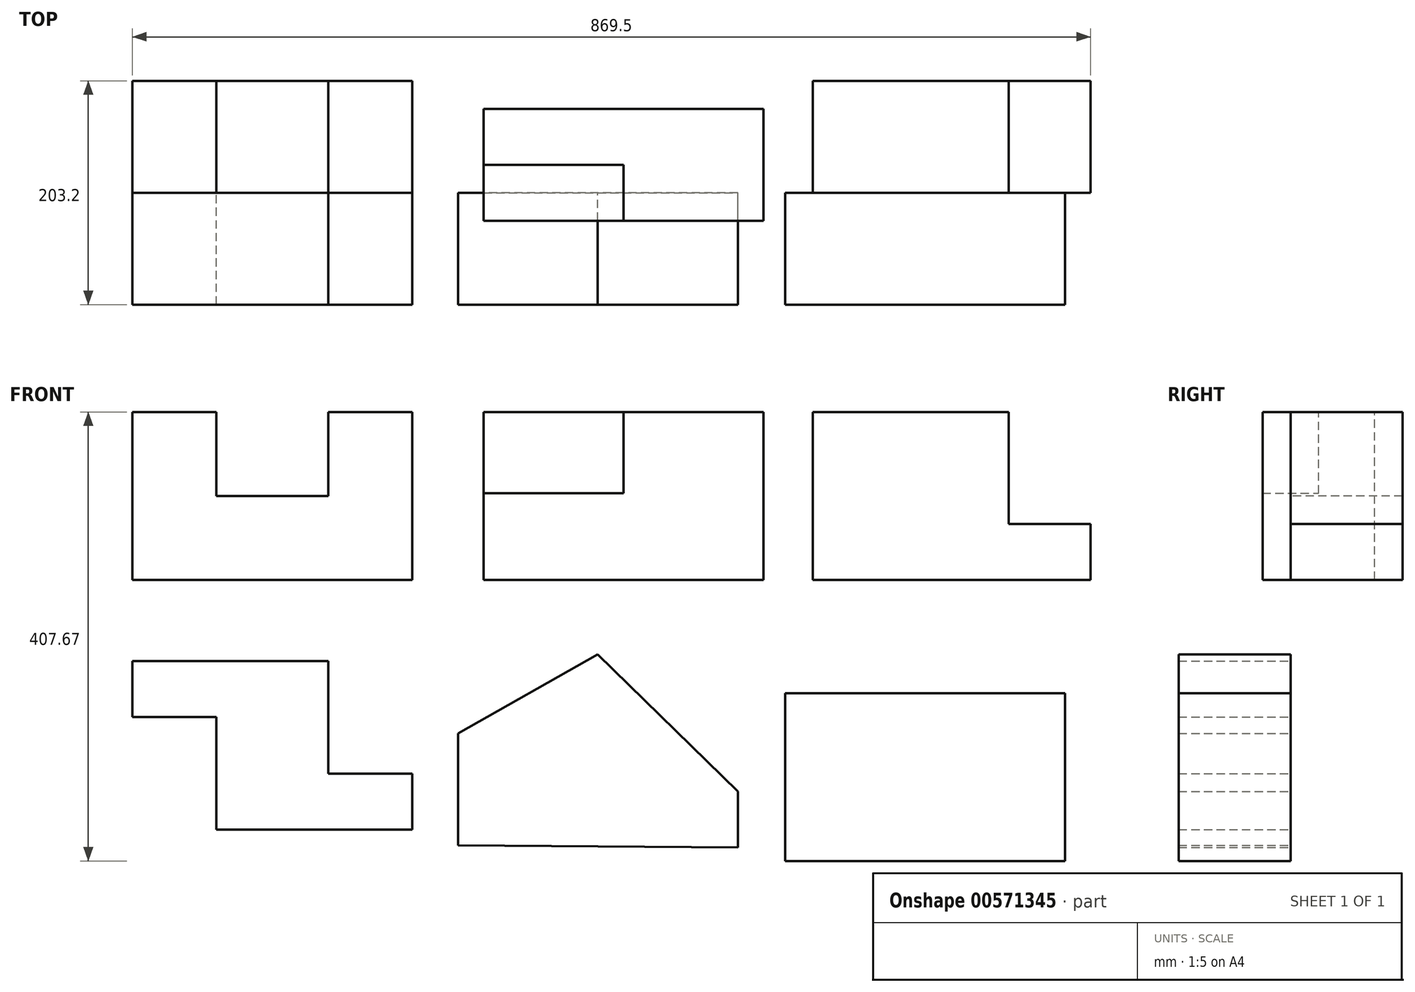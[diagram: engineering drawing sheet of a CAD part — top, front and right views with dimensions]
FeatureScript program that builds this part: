
annotation { "Feature Type Name" : "Feature", "Feature Type Description" : "" }
export const myFeature = defineFeature(function(context is Context, id is Id, definition is map)
    precondition{}
    {
        {
            var Q0;
            Q0=qCreatedBy(makeId("Front.planeOp"),FACE);
            var sketch = newSketch(context, id + "F0", { "sketchPlane" : qUnion([Q0])});
            skLineSegment(sketch, "E0", {"start": v(0, 0) * mm, "end": v(254, 0) * mm});
            skLineSegment(sketch, "E1", {"start": v(254, 0) * mm, "end": v(254, 152.4) * mm});
            skPoint(sketch, "E2.orphan", {"position": v(128.57, 246.94) * mm});
            skPoint(sketch, "E3.end.orphan", {"position": v(179.34, 246.94) * mm});
            skLineSegment(sketch, "E4", {"start": v(254, 152.4) * mm, "end": v(177.8, 152.4) * mm});
            skPoint(sketch, "E5.start.orphan", {"position": v(131.46, 152.4) * mm});
            skPoint(sketch, "E6.start.orphan", {"position": v(0, 189.1) * mm});
            skLineSegment(sketch, "E7", {"start": v(177.8, 152.4) * mm, "end": v(177.8, 76.2) * mm});
            skLineSegment(sketch, "E8", {"start": v(177.8, 76.2) * mm, "end": v(76.2, 76.2) * mm});
            skLineSegment(sketch, "E9", {"start": v(76.2, 76.2) * mm, "end": v(76.2, 152.4) * mm});
            skLineSegment(sketch, "E10", {"start": v(76.2, 152.4) * mm, "end": v(0, 152.4) * mm});
            skLineSegment(sketch, "E11", {"start": v(0, 152.4) * mm, "end": v(0, 0) * mm});
            skSolve(sketch);
        }
        {
            var Q0;
            Q0=makeQuery(id+"F0.imprint","IMPRINT",FACE,{"disambiguationData":[TD([[makeQuery(id+"F0.imprint","IMPRINT",EDGE,{"derivedFrom":sQuery(id+"F0.wireOp",EDGE,"E0")}),1.0]])]});
            extrude(context, id + "F1", {"entities" : qUnion([Q0]), "oppositeDirection" : true, "depth" : 101.6 * mm, "offsetDistance" : 25.4 * mm});
        }
        {
            var Q0;
            Q0=qCreatedBy(makeId("Front.planeOp"),FACE);
            var sketch = newSketch(context, id + "F2", { "sketchPlane" : qUnion([Q0])});
            skLineSegment(sketch, "E12.left", {"start": v(318.7, 0) * mm, "end": v(318.7, 0) * mm});
            skLineSegment(sketch, "E12.right", {"start": v(576, 0) * mm, "end": v(576, 0) * mm});
            skLineSegment(sketch, "E13.bottom", {"start": v(318.7, 0) * mm, "end": v(572.7, 0) * mm});
            skLineSegment(sketch, "E13.top", {"start": v(318.7, 152.4) * mm, "end": v(572.7, 152.4) * mm});
            skLineSegment(sketch, "E13.left", {"start": v(318.7, 0) * mm, "end": v(318.7, 152.4) * mm});
            skLineSegment(sketch, "E13.right", {"start": v(572.7, 0) * mm, "end": v(572.7, 152.4) * mm});
            skSolve(sketch);
        }
        {
            var Q0;
            Q0=makeQuery(id+"F2.imprint","IMPRINT",FACE,{"disambiguationData":[TD([[makeQuery(id+"F2.imprint","IMPRINT",EDGE,{"derivedFrom":sQuery(id+"F2.wireOp",EDGE,"E13.bottom")}),1.0]])]});
            extrude(context, id + "F3", {"entities" : qUnion([Q0]), "depth" : 25.4 * mm, "offsetDistance" : 25.4 * mm});
        }
        {
            var Q0;
            Q0=makeQuery(id+"F3.opExtrude","SWEPT_FACE",FACE,{"disambiguationData":[OSD([sQuery(id+"F2.wireOp",EDGE,"E13.top")])]});
            extrude(context, id + "F4", {"entities" : qUnion([Q0]), "operationType" : NewBodyOperationType.ADD, "oppositeDirection" : true, "depth" : 25.4 * mm, "offsetDistance" : 25.4 * mm});
        }
        {
            var Q0;
            Q0=makeQuery(id+"F3.opExtrude","CAP_FACE",FACE,{"disambiguationData":[OSD([sQuery(id+"F2.wireOp",EDGE,"E13.bottom"),sQuery(id+"F2.wireOp",EDGE,"E13.top"),sQuery(id+"F2.wireOp",EDGE,"E13.left"),sQuery(id+"F2.wireOp",EDGE,"E13.right")])],"isStart":false});
            extrude(context, id + "F5", {"entities" : qUnion([Q0]), "operationType" : NewBodyOperationType.ADD, "oppositeDirection" : true, "depth" : 101.6 * mm, "offsetDistance" : 25.4 * mm});
        }
        {
            var Q0;
            {var subQ0=sQuery(id+"F2.wireOp",EDGE,"E13.top");Q0=makeQuery(id+"F5.boolean.opBoolean","MERGE",FACE,{"derivedFrom":[makeQuery(id+"F3.opExtrude","SWEPT_FACE",FACE,{"disambiguationData":[OSD([subQ0])]}),makeQuery(id+"F5.opExtrude","SWEPT_FACE",FACE,{"disambiguationData":[OSD([subQ0])]})]});}
            var sketch = newSketch(context, id + "F6", { "sketchPlane" : qUnion([Q0])});
            skLineSegment(sketch, "E14.bottom", {"start": v(318.7, -25.4) * mm, "end": v(445.7, -25.4) * mm});
            skLineSegment(sketch, "E14.top", {"start": v(318.7, 25.4) * mm, "end": v(445.7, 25.4) * mm});
            skLineSegment(sketch, "E14.left", {"start": v(318.7, -25.4) * mm, "end": v(318.7, 25.4) * mm});
            skLineSegment(sketch, "E14.right", {"start": v(445.7, -25.4) * mm, "end": v(445.7, 25.4) * mm});
            skSolve(sketch);
        }
        {
            var Q0;
            Q0=makeQuery(id+"F6.imprint","IMPRINT",FACE,{"disambiguationData":[TD([[makeQuery(id+"F6.imprint","IMPRINT",EDGE,{"derivedFrom":sQuery(id+"F6.wireOp",EDGE,"E14.bottom")}),1.0]])]});
            extrude(context, id + "F7", {"entities" : qUnion([Q0]), "operationType" : NewBodyOperationType.REMOVE, "oppositeDirection" : true, "depth" : 73.9 * mm, "offsetDistance" : 25.4 * mm});
        }
        {
            var Q0;
            Q0=qCreatedBy(makeId("Front.planeOp"),FACE);
            var sketch = newSketch(context, id + "F8", { "sketchPlane" : qUnion([Q0])});
            skLineSegment(sketch, "E15", {"start": v(617.45, 0) * mm, "end": v(869.5, 0) * mm});
            skLineSegment(sketch, "E16", {"start": v(617.45, 0) * mm, "end": v(617.45, 152.4) * mm});
            skLineSegment(sketch, "E17", {"start": v(869.5, 0) * mm, "end": v(869.5, 50.8) * mm});
            skLineSegment(sketch, "E18", {"start": v(869.5, 50.8) * mm, "end": v(795.25, 50.8) * mm});
            skLineSegment(sketch, "E19", {"start": v(795.25, 50.8) * mm, "end": v(795.25, 152.4) * mm});
            skLineSegment(sketch, "E20", {"start": v(617.45, 152.4) * mm, "end": v(795.25, 152.4) * mm});
            skLineSegment(sketch, "E21", {"start": v(668.25, 152.4) * mm, "end": v(668.25, 0) * mm});
            skSolve(sketch);
        }
        {
            var Q0;
            {var subQ1=sQuery(id+"F8.wireOp",EDGE,"E17");Q0=makeQuery(id+"F8.imprint","IMPRINT",FACE,{"disambiguationData":[TD([[makeQuery(id+"F8.imprint","IMPRINT",EDGE,{"derivedFrom":subQ1}),1.0]])]});}
            var Q1;
            {var subQ0=sQuery(id+"F8.wireOp",EDGE,"E16");Q1=makeQuery(id+"F8.imprint","IMPRINT",FACE,{"disambiguationData":[TD([[makeQuery(id+"F8.imprint","IMPRINT",EDGE,{"derivedFrom":subQ0}),-1.0]])]});}
            extrude(context, id + "F9", {"entities" : qUnion([Q0, Q1]), "oppositeDirection" : true, "depth" : 101.6 * mm, "offsetDistance" : 25.4 * mm});
        }
        {
            var Q0;
            Q0=qCreatedBy(makeId("Front.planeOp"),FACE);
            var sketch = newSketch(context, id + "F10", { "sketchPlane" : qUnion([Q0])});
            skPoint(sketch, "E22.start.orphan", {"position": v(0, -73.9) * mm});
            skLineSegment(sketch, "E23", {"start": v(0, -73.9) * mm, "end": v(177.8, -73.9) * mm});
            skLineSegment(sketch, "E24", {"start": v(177.8, -73.9) * mm, "end": v(177.8, -176.1) * mm});
            skLineSegment(sketch, "E25", {"start": v(177.8, -176.1) * mm, "end": v(254, -176.1) * mm});
            skLineSegment(sketch, "E26", {"start": v(254, -176.1) * mm, "end": v(254, -226.9) * mm});
            skLineSegment(sketch, "E27", {"start": v(254, -226.9) * mm, "end": v(76.2, -226.9) * mm});
            skLineSegment(sketch, "E28", {"start": v(76.2, -226.9) * mm, "end": v(76.2, -124.7) * mm});
            skLineSegment(sketch, "E29", {"start": v(76.2, -124.7) * mm, "end": v(0, -124.7) * mm});
            skLineSegment(sketch, "E30", {"start": v(0, -124.7) * mm, "end": v(0, -73.9) * mm});
            skSolve(sketch);
        }
        {
            var Q0;
            Q0=makeQuery(id+"F10.imprint","IMPRINT",FACE,{"disambiguationData":[TD([[makeQuery(id+"F10.imprint","IMPRINT",EDGE,{"derivedFrom":sQuery(id+"F10.wireOp",EDGE,"E23")}),-1.0]])]});
            extrude(context, id + "F11", {"entities" : qUnion([Q0]), "depth" : 101.6 * mm, "offsetDistance" : 25.4 * mm});
        }
        {
            var Q0;
            Q0=qCreatedBy(makeId("Front.planeOp"),FACE);
            var sketch = newSketch(context, id + "F12", { "sketchPlane" : qUnion([Q0])});
            skLineSegment(sketch, "E31", {"start": v(295.5, -241.18) * mm, "end": v(295.5, -139.58) * mm});
            skLineSegment(sketch, "E32", {"start": v(295.5, -139.58) * mm, "end": v(422.27, -67.8) * mm});
            skLineSegment(sketch, "E33", {"start": v(422.27, -67.8) * mm, "end": v(549.5, -192.17) * mm});
            skLineSegment(sketch, "E34", {"start": v(549.5, -192.17) * mm, "end": v(549.5, -242.97) * mm});
            skLineSegment(sketch, "E35", {"start": v(549.5, -242.97) * mm, "end": v(295.5, -241.18) * mm});
            skSolve(sketch);
        }
        {
            var Q0;
            Q0=makeQuery(id+"F12.imprint","IMPRINT",FACE,{"disambiguationData":[TD([[makeQuery(id+"F12.imprint","IMPRINT",EDGE,{"derivedFrom":sQuery(id+"F12.wireOp",EDGE,"E31")}),-1.0]])]});
            extrude(context, id + "F13", {"entities" : qUnion([Q0]), "depth" : 101.6 * mm, "offsetDistance" : 25.4 * mm});
        }
        {
            var Q0;
            Q0=qCreatedBy(makeId("Front.planeOp"),FACE);
            var sketch = newSketch(context, id + "F14", { "sketchPlane" : qUnion([Q0])});
            skLineSegment(sketch, "E36.bottom", {"start": v(592.25, -255.27) * mm, "end": v(846.25, -255.27) * mm});
            skLineSegment(sketch, "E36.top", {"start": v(592.25, -102.87) * mm, "end": v(846.25, -102.87) * mm});
            skLineSegment(sketch, "E36.left", {"start": v(592.25, -255.27) * mm, "end": v(592.25, -102.87) * mm});
            skLineSegment(sketch, "E36.right", {"start": v(846.25, -255.27) * mm, "end": v(846.25, -102.87) * mm});
            skLineSegment(sketch, "E37.bottom", {"start": v(617.65, -229.87) * mm, "end": v(820.85, -229.87) * mm});
            skLineSegment(sketch, "E37.top", {"start": v(617.65, -128.27) * mm, "end": v(820.85, -128.27) * mm});
            skLineSegment(sketch, "E37.left", {"start": v(617.65, -229.87) * mm, "end": v(617.65, -128.27) * mm});
            skLineSegment(sketch, "E37.right", {"start": v(820.85, -229.87) * mm, "end": v(820.85, -128.27) * mm});
            skSolve(sketch);
        }
        {
            var Q0;
            Q0 = qSketchRegion(id + "F14", true);
            var Q1;
            Q1=makeQuery(id+"F14.imprint","IMPRINT",FACE,{"disambiguationData":[TD([[makeQuery(id+"F14.imprint","IMPRINT",EDGE,{"derivedFrom":sQuery(id+"F14.wireOp",EDGE,"E37.bottom")}),1.0]])]});
            extrude(context, id + "F15", {"entities" : qUnion([Q0, Q1]), "depth" : 101.6 * mm, "offsetDistance" : 25.4 * mm});
        }
    });
